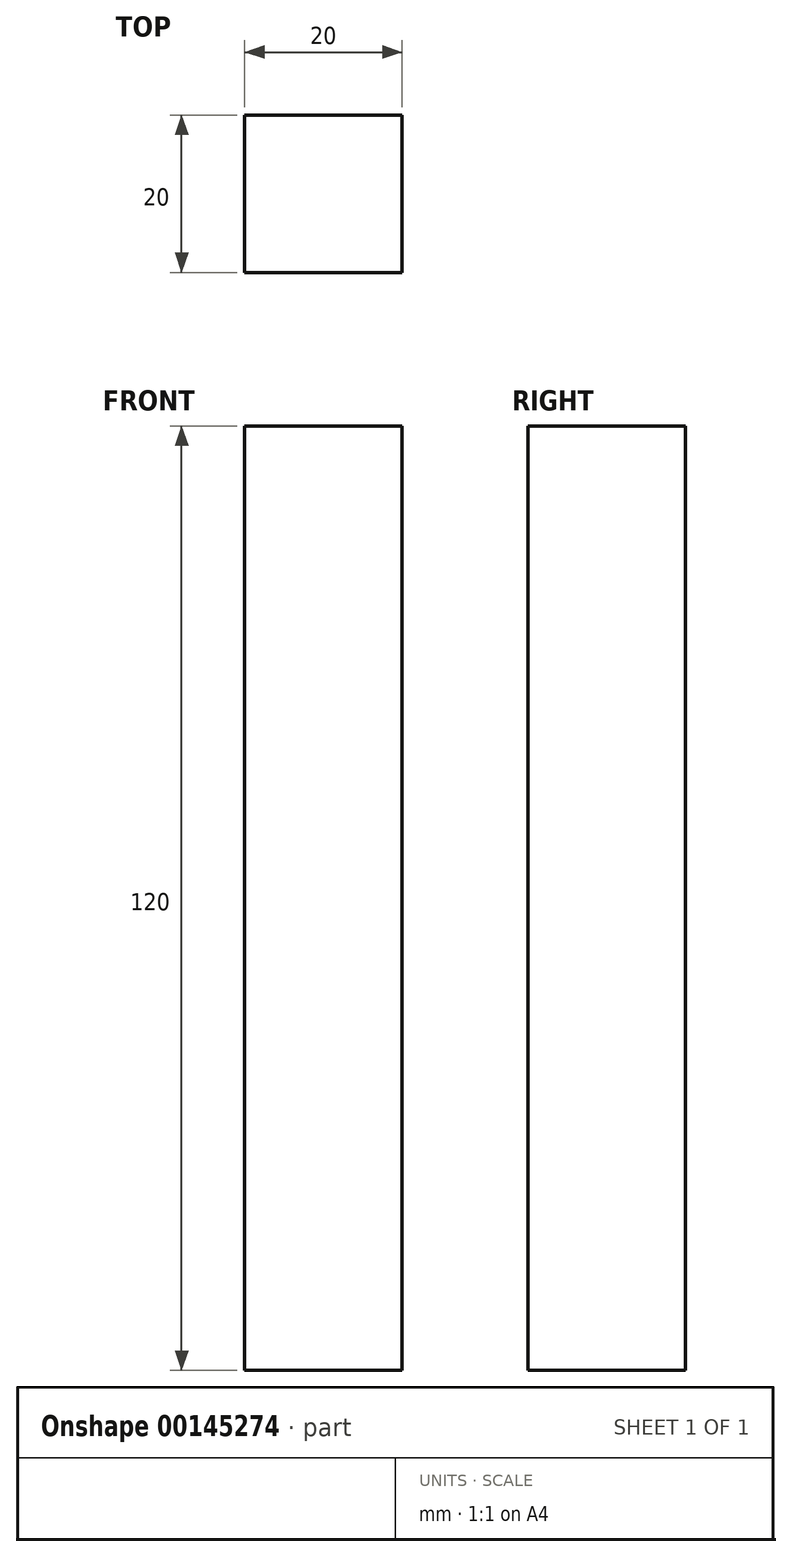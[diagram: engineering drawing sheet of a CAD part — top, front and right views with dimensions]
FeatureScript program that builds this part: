
annotation { "Feature Type Name" : "Feature", "Feature Type Description" : "" }
export const myFeature = defineFeature(function(context is Context, id is Id, definition is map)
    precondition{}
    {
        {
            var Q0;
            Q0=qCreatedBy(makeId("Top.planeOp"),FACE);
            var sketch = newSketch(context, id + "F0", { "sketchPlane" : qUnion([Q0])});
            skLineSegment(sketch, "E0.bottom", {"start": v(10, 10) * mm, "end": v(-10, 10) * mm});
            skLineSegment(sketch, "E0.top", {"start": v(10, -10) * mm, "end": v(-10, -10) * mm});
            skLineSegment(sketch, "E0.left", {"start": v(10, 10) * mm, "end": v(10, -10) * mm});
            skLineSegment(sketch, "E0.right", {"start": v(-10, 10) * mm, "end": v(-10, -10) * mm});
            skPoint(sketch, "E0.middle", {"position": v(0, 0) * mm});
            skSolve(sketch);
        }
        {
            var Q0;
            Q0=sQuery(id+"F0.wireOp",EDGE,"E0.top");
            var Q1;
            Q1=sQuery(id+"F0.wireOp",EDGE,"E0.left");
            var Q2;
            Q2=sQuery(id+"F0.wireOp",EDGE,"E0.bottom");
            var Q3;
            Q3=sQuery(id+"F0.wireOp",EDGE,"E0.right");
            extrude(context, id + "F1", {"bodyType" : ToolBodyType.SURFACE, "surfaceEntities" : qUnion([Q0, Q1, Q2, Q3]), "depth" : 120 * mm});
        }
    });
